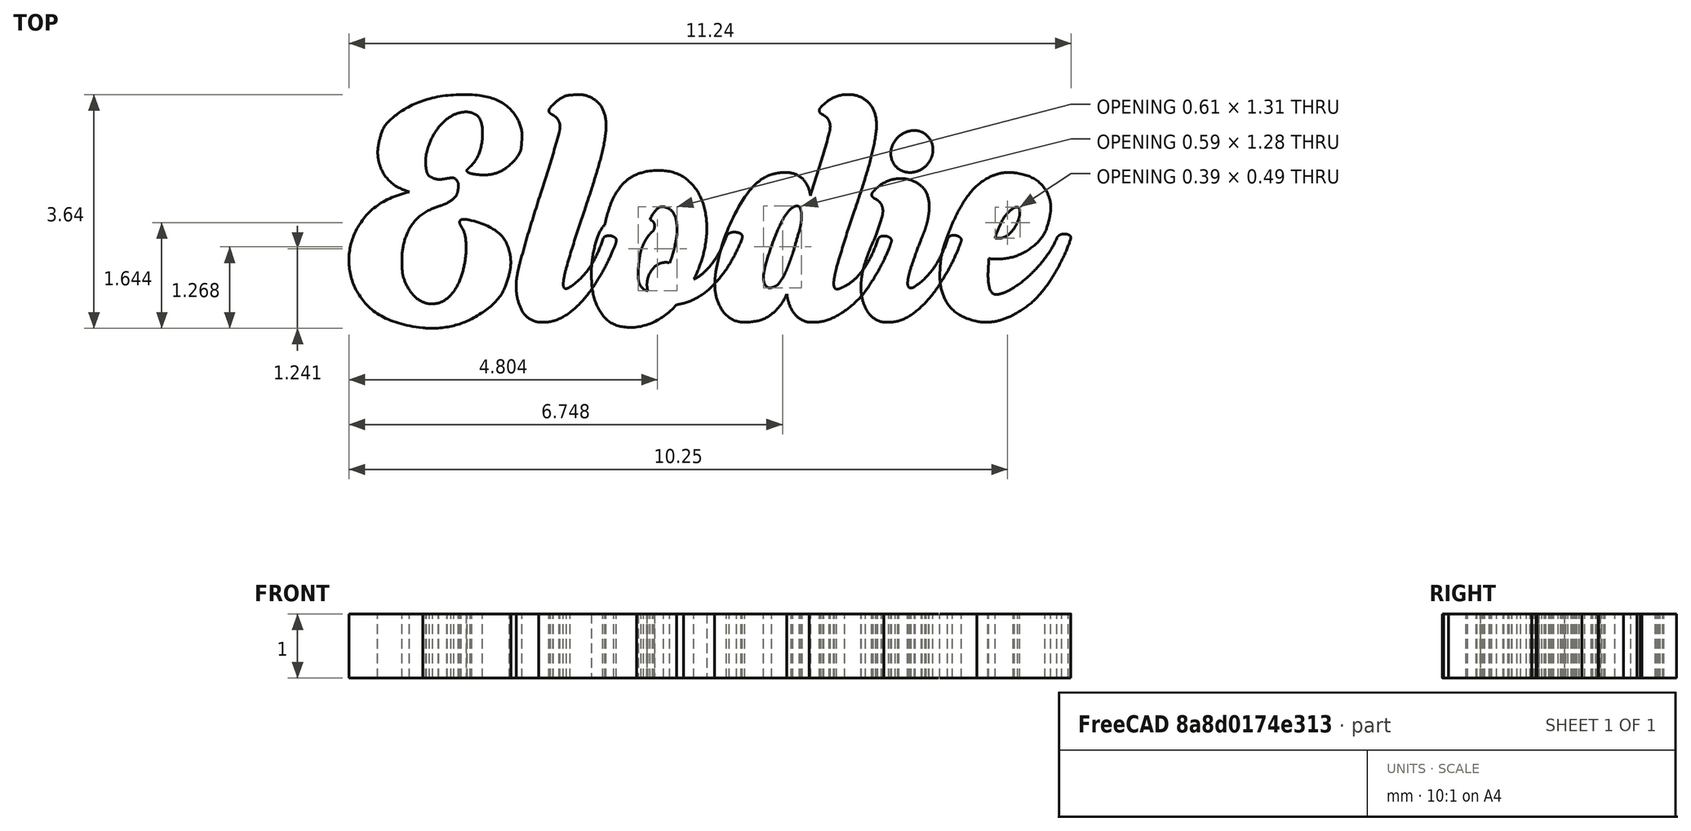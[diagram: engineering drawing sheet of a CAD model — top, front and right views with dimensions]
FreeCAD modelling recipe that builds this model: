
FCSTD DOCUMENT  (FreeCAD 0.18R16131 (Git))
Label: elodie
License: All rights reserved
LicenseURL: http://en.wikipedia.org/wiki/All_rights_reserved
objects: Part::Extrusion×2, Part::Part2DObjectPython×1
note: 3 computed .brp shape members not serialized (recipe doc carries the construction recipe); baked Part::Feature solids carry a one-line shape summary decoded from their .brp

FEATURE [Part::Part2DObjectPython] ShapeString  # Draft 2D object (typed FeaturePython)
  FontFile = <path>
  Size = 4
  String = Elodie
  Tracking = 0
FEATURE [Part::Extrusion] Extrude
  Base = -> ShapeString
  Dir = (0,0,1)
  DirMode = 2
  FaceMakerClass = Part::FaceMakerBullseye
  LengthFwd = 1
  LengthRev = 0
  Solid = false
  Symmetric = false
FEATURE [Part::Extrusion] Extrude001
  Base = -> ShapeString
  Dir = (0,0,1)
  DirMode = 2
  FaceMakerClass = Part::FaceMakerBullseye
  LengthFwd = 1
  LengthRev = 0
  Solid = false
  Symmetric = false
note: 1 file-system path scrubbed to <path> (originals preserved in the JSON sidecar)
